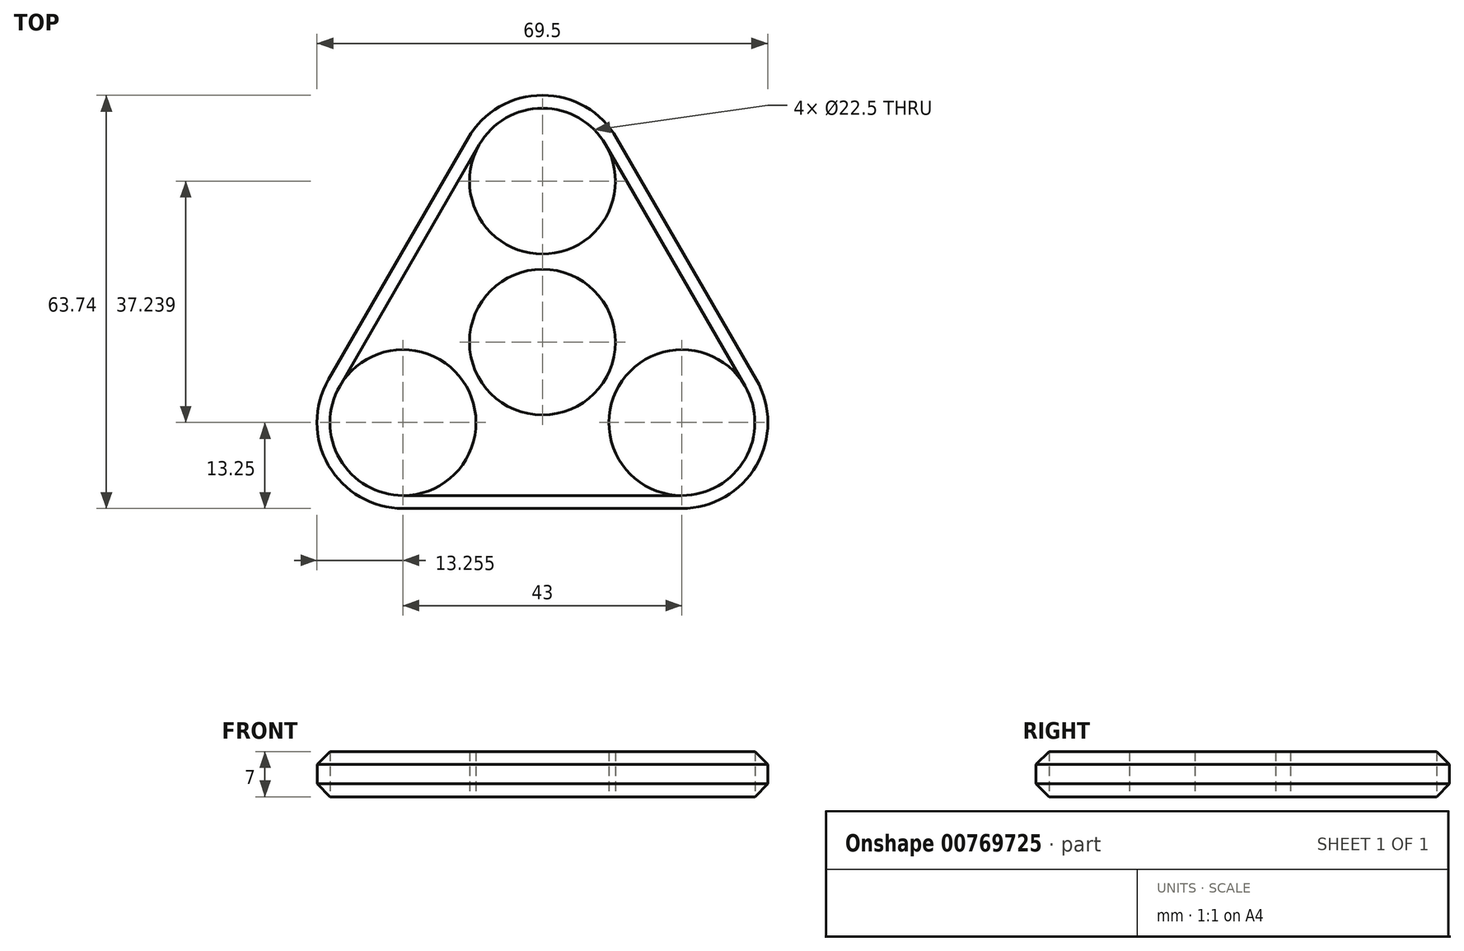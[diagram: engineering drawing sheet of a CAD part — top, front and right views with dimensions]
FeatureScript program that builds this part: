
annotation { "Feature Type Name" : "Feature", "Feature Type Description" : "" }
export const myFeature = defineFeature(function(context is Context, id is Id, definition is map)
    precondition{}
    {
        {
            var Q0;
            Q0=qCreatedBy(makeId("Top.planeOp"),FACE);
            var sketch = newSketch(context, id + "F0", { "sketchPlane" : qUnion([Q0])});
            skLineSegment(sketch, "E0", {"start": v(-10.03, 0) * mm, "end": v(32.97, 0) * mm, "construction": true});
            skLineSegment(sketch, "E1", {"start": v(32.97, 0) * mm, "end": v(11.47, 37.24) * mm, "construction": true});
            skLineSegment(sketch, "E2", {"start": v(11.47, 37.24) * mm, "end": v(-10.03, 0) * mm, "construction": true});
            skCircle(sketch, "E3", {"center": v(32.97, 0) * mm, "radius": 11.25 * mm});
            skCircle(sketch, "E4", {"center": v(11.47, 37.24) * mm, "radius": 11.25 * mm});
            skCircle(sketch, "E5", {"center": v(-10.03, 0) * mm, "radius": 11.25 * mm});
            skPoint(sketch, "E6", {"position": v(0.72, 18.62) * mm});
            skPoint(sketch, "E7", {"position": v(22.22, 18.62) * mm});
            skPoint(sketch, "E8", {"position": v(11.47, 0) * mm});
            skLineSegment(sketch, "E9", {"start": v(11.47, 37.24) * mm, "end": v(11.47, 0) * mm, "construction": true});
            skLineSegment(sketch, "E10", {"start": v(0.72, 18.62) * mm, "end": v(32.97, 0) * mm, "construction": true});
            skLineSegment(sketch, "E11", {"start": v(22.22, 18.62) * mm, "end": v(-10.03, 0) * mm, "construction": true});
            skPoint(sketch, "E12", {"position": v(11.47, 12.41) * mm});
            skCircle(sketch, "E13", {"center": v(11.47, 12.41) * mm, "radius": 11.25 * mm});
            skArc(sketch, "E14.0", {"start": v(16.1, 24.83) * mm, "mid": v(11.47, 50.49) * mm, "end": v(6.84, 24.83) * mm});
            skArc(sketch, "E15.0", {"start": v(3.04, 2.2) * mm, "mid": v(11.47, -0.84) * mm, "end": v(19.9, 2.2) * mm});
            skArc(sketch, "E16.0", {"start": v(-1.6, 10.22) * mm, "mid": v(-21.5, -6.63) * mm, "end": v(3.04, 2.2) * mm});
            skArc(sketch, "E17.0", {"start": v(19.9, 2.2) * mm, "mid": v(44.45, -6.63) * mm, "end": v(24.54, 10.22) * mm});
            skLineSegment(sketch, "E18", {"start": v(0.72, 18.62) * mm, "end": v(0, 19.04) * mm, "construction": true});
            skLineSegment(sketch, "E19", {"start": v(11.47, 0) * mm, "end": v(11.47, -0.84) * mm, "construction": true});
            skLineSegment(sketch, "E20", {"start": v(22.22, 18.62) * mm, "end": v(22.95, 19.04) * mm, "construction": true});
            skLineSegment(sketch, "E21", {"start": v(2.4, 27.2) * mm, "end": v(2.55, 27.45) * mm});
            skArc(sketch, "E22.trimOffspring", {"start": v(24.54, 10.22) * mm, "mid": v(22.95, 19.04) * mm, "end": v(16.1, 24.83) * mm});
            skArc(sketch, "E23.trimOffspring", {"start": v(6.84, 24.83) * mm, "mid": v(0, 19.04) * mm, "end": v(-1.6, 10.22) * mm});
            skLineSegment(sketch, "E24", {"start": v(-10.03, 0) * mm, "end": v(-19.77, 5.62) * mm});
            skLineSegment(sketch, "E25", {"start": v(11.47, 37.24) * mm, "end": v(1.73, 42.86) * mm});
            skLineSegment(sketch, "E26", {"start": v(0, 43.86) * mm, "end": v(-21.5, 6.62) * mm});
            skLineSegment(sketch, "E27", {"start": v(-10.03, 0) * mm, "end": v(-10.03, -11.25) * mm});
            skLineSegment(sketch, "E28", {"start": v(32.97, -13.25) * mm, "end": v(-10.03, -13.25) * mm});
            skLineSegment(sketch, "E29", {"start": v(32.97, 0) * mm, "end": v(32.97, -11.25) * mm});
            skLineSegment(sketch, "E30", {"start": v(32.97, 0) * mm, "end": v(44.45, 6.62) * mm});
            skLineSegment(sketch, "E31", {"start": v(44.45, 6.62) * mm, "end": v(22.95, 43.86) * mm});
            skSolve(sketch);
        }
        {
            var Q0;
            Q0=makeQuery(id+"F0.imprint","IMPRINT",FACE,{"disambiguationData":[TD([[makeQuery(id+"F0.imprint","IMPRINT",EDGE,{"derivedFrom":sQuery(id+"F0.wireOp",EDGE,"E3")}),-1.0]])]});
            var Q1;
            Q1=makeQuery(id+"F0.imprint","IMPRINT",FACE,{"disambiguationData":[TD([[makeQuery(id+"F0.imprint","IMPRINT",EDGE,{"derivedFrom":sQuery(id+"F0.wireOp",EDGE,"E4")}),-1.0]])]});
            var Q2;
            {var subQ0=sQuery(id+"F0.wireOp",EDGE,"E24");var subQ1=sQuery(id+"F0.wireOp",EDGE,"E5");var subQ2=makeQuery(id+"F0.imprint","INTERSECT",VERTEX,{"derivedFrom":[subQ1,subQ0]});Q2=makeQuery(id+"F0.imprint","IMPRINT",FACE,{"disambiguationData":[TD([[makeQuery(id+"F0.imprint","IMPRINT",EDGE,{"disambiguationData":[TD([[subQ2,-1.0]])],"derivedFrom":subQ1}),-1.0]])]});}
            var Q3;
            {var subQ0=sQuery(id+"F0.wireOp",EDGE,"gPQNnEgg-kcM0-zcSx-1lDJ-uuy41ka0ClYo");Q3=makeQuery(id+"F0.imprint","IMPRINT",FACE,{"disambiguationData":[TD([[makeQuery(id+"F0.imprint","IMPRINT",EDGE,{"derivedFrom":subQ0}),-1.0]])]});}
            var Q4;
            {var subQ3=sQuery(id+"F0.wireOp",EDGE,"vSuc5ejM-Uw8A-PQrc-03Ul-SzUVSElhu1BX");Q4=makeQuery(id+"F0.imprint","IMPRINT",FACE,{"disambiguationData":[TD([[makeQuery(id+"F0.imprint","IMPRINT",EDGE,{"derivedFrom":subQ3}),1.0]])]});}
            var Q5;
            {var subQ0=sQuery(id+"F0.wireOp",EDGE,"ukXwWn0Q-RDmQ-V7ra-tZfT-tII8dwk7K9Fi");Q5=makeQuery(id+"F0.imprint","IMPRINT",FACE,{"disambiguationData":[TD([[makeQuery(id+"F0.imprint","IMPRINT",EDGE,{"derivedFrom":subQ0}),1.0]])]});}
            var Q6;
            {var subQ0=sQuery(id+"F0.wireOp",EDGE,"E23.trimOffspring");Q6=makeQuery(id+"F0.imprint","IMPRINT",FACE,{"disambiguationData":[TD([[makeQuery(id+"F0.imprint","IMPRINT",EDGE,{"derivedFrom":subQ0}),-1.0]])]});}
            var Q7;
            {var subQ0=sQuery(id+"F0.wireOp",EDGE,"E22.trimOffspring");Q7=makeQuery(id+"F0.imprint","IMPRINT",FACE,{"disambiguationData":[TD([[makeQuery(id+"F0.imprint","IMPRINT",EDGE,{"derivedFrom":subQ0}),-1.0]])]});}
            var Q8;
            {var subQ0=sQuery(id+"F0.wireOp",EDGE,"E15.0");Q8=makeQuery(id+"F0.imprint","IMPRINT",FACE,{"disambiguationData":[TD([[makeQuery(id+"F0.imprint","IMPRINT",EDGE,{"derivedFrom":subQ0}),-1.0]])]});}
            extrude(context, id + "F1", {"entities" : qUnion([Q0, Q1, Q2, Q3, Q4, Q5, Q6, Q7, Q8]), "depth" : 7 * mm, "offsetDistance" : 25 * mm});
        }
        {
            var Q0;
            Q0=makeQuery(id+"F1.opExtrude","CAP_EDGE",EDGE,{"disambiguationData":[OSD([sQuery(id+"F0.wireOp",EDGE,"E31")])],"isStart":true});
            var Q1;
            Q1=makeQuery(id+"F1.opExtrude","CAP_EDGE",EDGE,{"disambiguationData":[OSD([sQuery(id+"F0.wireOp",EDGE,"E17.0")])],"isStart":true});
            var Q2;
            Q2=makeQuery(id+"F1.opExtrude","CAP_EDGE",EDGE,{"disambiguationData":[OSD([sQuery(id+"F0.wireOp",EDGE,"E28")])],"isStart":true});
            var Q3;
            Q3=makeQuery(id+"F1.opExtrude","CAP_EDGE",EDGE,{"disambiguationData":[OSD([sQuery(id+"F0.wireOp",EDGE,"E16.0")])],"isStart":true});
            var Q4;
            Q4=makeQuery(id+"F1.opExtrude","CAP_EDGE",EDGE,{"disambiguationData":[OSD([sQuery(id+"F0.wireOp",EDGE,"E26")])],"isStart":true});
            var Q5;
            Q5=makeQuery(id+"F1.opExtrude","CAP_EDGE",EDGE,{"disambiguationData":[OSD([sQuery(id+"F0.wireOp",EDGE,"E14.0")])],"isStart":true});
            var Q6;
            Q6=makeQuery(id+"F1.opExtrude","CAP_EDGE",EDGE,{"disambiguationData":[OSD([sQuery(id+"F0.wireOp",EDGE,"E26")])],"isStart":false});
            chamfer(context, id + "F2", {"entities" : qUnion([Q0, Q1, Q2, Q3, Q4, Q5, Q6]), "width" : 2 * mm, "tangentPropagation" : true});
        }
    });
